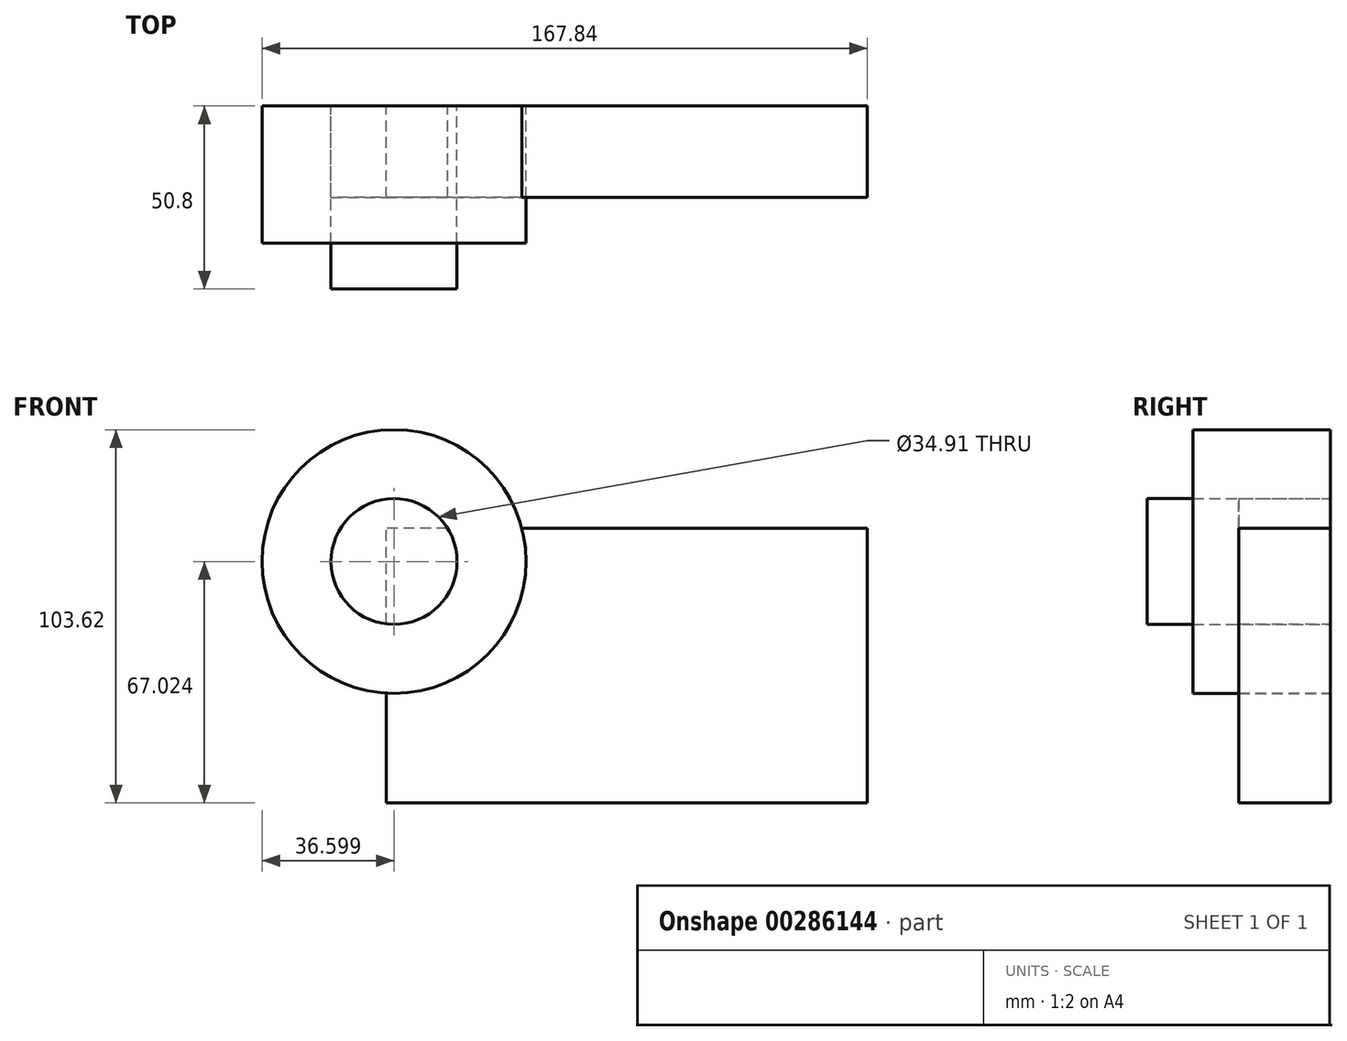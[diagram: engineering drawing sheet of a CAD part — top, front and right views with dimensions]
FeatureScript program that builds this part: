
annotation { "Feature Type Name" : "Feature", "Feature Type Description" : "" }
export const myFeature = defineFeature(function(context is Context, id is Id, definition is map)
    precondition{}
    {
        {
            var Q0;
            Q0=qCreatedBy(makeId("Front.planeOp"),FACE);
            var sketch = newSketch(context, id + "F0", { "sketchPlane" : qUnion([Q0])});
            skLineSegment(sketch, "E0.bottom", {"start": v(0, 0) * mm, "end": v(-133.35, 0) * mm});
            skLineSegment(sketch, "E0.top", {"start": v(0, 76.2) * mm, "end": v(-133.35, 76.2) * mm});
            skLineSegment(sketch, "E0.left", {"start": v(0, 0) * mm, "end": v(0, 76.2) * mm});
            skLineSegment(sketch, "E0.right", {"start": v(-133.35, 0) * mm, "end": v(-133.35, 76.2) * mm});
            skCircle(sketch, "E1", {"center": v(-131.24, 67.02) * mm, "radius": 36.6 * mm});
            skCircle(sketch, "E2", {"center": v(-131.24, 67.02) * mm, "radius": 17.46 * mm});
            skEllipse(sketch, "E3", {"center": v(-216.62, 103) * mm, "majorRadius": 30.34 * mm, "minorRadius": 15.48 * mm, "majorAxis": v(1, 0)});
            skLineSegment(sketch, "E4", {"start": v(-218.7, 75.96) * mm, "end": v(-218.7, 76.2) * mm});
            skLineSegment(sketch, "E5", {"start": v(-159.57, 76.2) * mm, "end": v(-159.57, 75.96) * mm});
            skSolve(sketch);
        }
        {
            var Q0;
            Q0=makeQuery(id+"F0.imprint","IMPRINT",FACE,{"disambiguationData":[TD([[makeQuery(id+"F0.imprint","IMPRINT",EDGE,{"derivedFrom":sQuery(id+"F0.wireOp",EDGE,"E0.bottom")}),-1.0]])]});
            var Q1;
            {var subQ0=sQuery(id+"F0.wireOp",EDGE,"nYiPWvHE-ZhzR-HQ1y-aYms-Sgn45DEzKLA5");Q1=makeQuery(id+"F0.imprint","IMPRINT",FACE,{"disambiguationData":[TD([[makeQuery(id+"F0.imprint","IMPRINT",EDGE,{"derivedFrom":subQ0}),-1.0]])]});}
            var Q2;
            {var subQ0=sQuery(id+"F0.wireOp",EDGE,"E5");var subQ1=sQuery(id+"F0.wireOp",EDGE,"E0.top");var subQ2=makeQuery(id+"F0.imprint","INTERSECT",VERTEX,{"derivedFrom":[subQ1,subQ0]});Q2=makeQuery(id+"F0.imprint","IMPRINT",FACE,{"disambiguationData":[TD([[makeQuery(id+"F0.imprint","IMPRINT",EDGE,{"disambiguationData":[TD([[subQ2,-1.0]])],"derivedFrom":subQ1}),-1.0]])]});}
            var Q3;
            {var subQ0=sQuery(id+"F0.wireOp",EDGE,"E5");var subQ1=sQuery(id+"F0.wireOp",EDGE,"E0.top");var subQ2=makeQuery(id+"F0.imprint","INTERSECT",VERTEX,{"derivedFrom":[subQ1,subQ0]});Q3=makeQuery(id+"F0.imprint","IMPRINT",FACE,{"disambiguationData":[TD([[makeQuery(id+"F0.imprint","IMPRINT",EDGE,{"disambiguationData":[TD([[subQ2,1.0]])],"derivedFrom":subQ1}),-1.0]])]});}
            extrude(context, id + "F1", {"entities" : qUnion([Q0, Q1, Q2, Q3]), "depth" : 25.4 * mm});
        }
        {
            var Q0;
            Q0=sQuery(id+"F0.wireOp",EDGE,"E2");
            extrude(context, id + "F2", {"bodyType" : ToolBodyType.SURFACE, "surfaceEntities" : qUnion([Q0]), "depth" : 25.4 * mm});
        }
        {
            var Q0;
            Q0=makeQuery(id+"F0.imprint","IMPRINT",FACE,{"disambiguationData":[TD([[makeQuery(id+"F0.imprint","IMPRINT",EDGE,{"derivedFrom":sQuery(id+"F0.wireOp",EDGE,"E2")}),1.0]])]});
            extrude(context, id + "F3", {"entities" : qUnion([Q0]), "depth" : 50.8 * mm});
        }
        {
            var Q0;
            Q0=makeQuery(id+"F0.imprint","IMPRINT",FACE,{"disambiguationData":[TD([[makeQuery(id+"F0.imprint","IMPRINT",EDGE,{"derivedFrom":sQuery(id+"F0.wireOp",EDGE,"E1")}),1.0]])]});
            extrude(context, id + "F4", {"entities" : qUnion([Q0]), "depth" : 38.1 * mm});
        }
        {
            var Q0;
            Q0=qCreatedBy(makeId("Top.planeOp"),FACE);
            var sketch = newSketch(context, id + "F5", { "sketchPlane" : qUnion([Q0])});
            skCircle(sketch, "E6", {"center": v(-94.95, -11.52) * mm, "radius": 7.23 * mm});
            skSolve(sketch);
        }
        {
            var Q0;
            Q0=sQuery(id+"F5.wireOp",EDGE,"E6");
            extrude(context, id + "F6", {"bodyType" : ToolBodyType.SURFACE, "surfaceEntities" : qUnion([Q0]), "depth" : 25.4 * mm});
        }
    });
